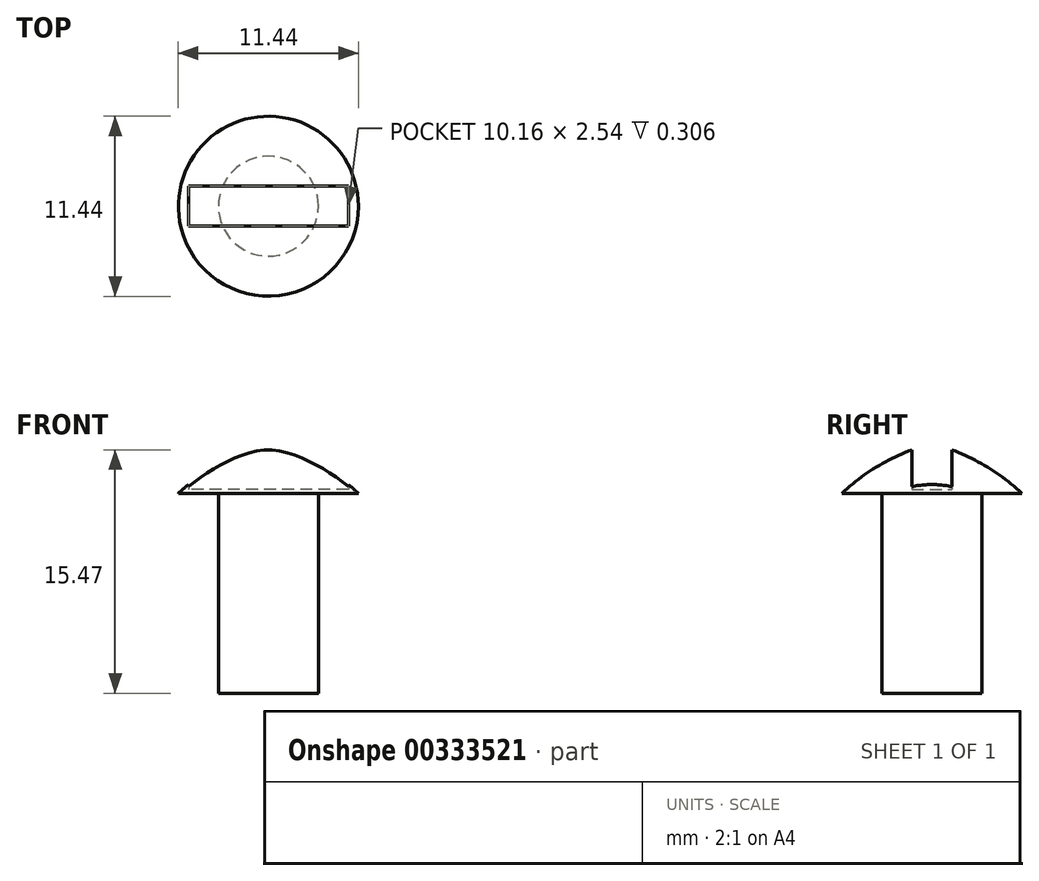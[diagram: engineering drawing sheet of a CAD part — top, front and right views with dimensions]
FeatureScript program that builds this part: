
annotation { "Feature Type Name" : "Feature", "Feature Type Description" : "" }
export const myFeature = defineFeature(function(context is Context, id is Id, definition is map)
    precondition{}
    {
        {
            var Q0;
            Q0=qCreatedBy(makeId("Front.planeOp"),FACE);
            var sketch = newSketch(context, id + "F0", { "sketchPlane" : qUnion([Q0])});
            skLineSegment(sketch, "E0", {"start": v(3.17, 0) * mm, "end": v(3.18, -12.7) * mm});
            skLineSegment(sketch, "E1", {"start": v(3.18, -12.7) * mm, "end": v(0, -12.7) * mm});
            skLineSegment(sketch, "E2", {"start": v(3.17, 0) * mm, "end": v(5.72, 0) * mm});
            skArc(sketch, "E3", {"start": v(5.72, 0) * mm, "mid": v(3.06, 1.95) * mm, "end": v(0, 3.18) * mm});
            skLineSegment(sketch, "E4", {"start": v(0, 3.17) * mm, "end": v(0, -12.7) * mm});
            skSolve(sketch);
        }
        {
            var Q0;
            Q0 = qSketchRegion(id + "F0", true);
            var Q1;
            Q1=sQuery(id+"F0.wireOp",EDGE,"E4");
            revolve(context, id + "F1", {"entities" : qUnion([Q0]), "axis" : qUnion([Q1]), "revolveType" : RevolveType.FULL});
        }
        {
            var Q0;
            Q0=qCreatedBy(makeId("Top.planeOp"),FACE);
            cPlane(context, id + "F2", {"entities" : qUnion([Q0]), "cplaneType" : CPlaneType.OFFSET, "offset" : 0.25 * mm, "width" : 152.4 * mm, "height" : 152.4 * mm});
        }
        {
            var Q0;
            Q0=qCreatedBy(id+"F2.planeOp",FACE);
            var sketch = newSketch(context, id + "F3", { "sketchPlane" : qUnion([Q0])});
            skLineSegment(sketch, "E5.bottom", {"start": v(5.08, -1.27) * mm, "end": v(-5.08, -1.27) * mm});
            skLineSegment(sketch, "E5.top", {"start": v(5.08, 1.27) * mm, "end": v(-5.08, 1.27) * mm});
            skLineSegment(sketch, "E5.left", {"start": v(5.08, -1.27) * mm, "end": v(5.08, 1.27) * mm});
            skLineSegment(sketch, "E5.right", {"start": v(-5.08, -1.27) * mm, "end": v(-5.08, 1.27) * mm});
            skPoint(sketch, "E5.middle", {"position": v(0, 0) * mm});
            skSolve(sketch);
        }
        {
            var Q0;
            Q0 = qSketchRegion(id + "F3", true);
            extrude(context, id + "F4", {"entities" : qUnion([Q0]), "operationType" : NewBodyOperationType.REMOVE, "endBound" : BoundingType.THROUGH_ALL, "depth" : 25.4 * mm, "offsetDistance" : 25.4 * mm});
        }
    });
